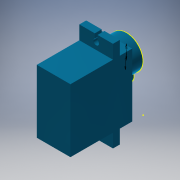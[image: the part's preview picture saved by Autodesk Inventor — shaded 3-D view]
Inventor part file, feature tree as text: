
AUTODESK INVENTOR PART (.ipt)
format: ipt  version: 2016 SP2 (Build 200236200, 236)  size: 158,208 bytes
history: native  units: mm
features: sketch x5, projected_geometry x5, extrude x4, plane x1, mirror x1
ambient origin geometry x8: Origin, YZ Plane, XZ Plane, XY Plane, X Axis, Y Axis, Z Axis, Center Point
bodies: Solid1 (feature_tree)
feature tree (16):
  extrude  "Extrusion1"  Depth=23.0mm
  extrude  "Extrusion2"  Depth=4.5mm
  extrude  "Extrusion3"  Depth=5.0mm TaperAngle=0.0deg
  plane  "Work Plane1"
  mirror  "Mirror1"
  extrude  "Extrusion4"  Depth=2.0mm
  sketch  "Sketch5"  dims[d10=0.5mm d11=3.5mm d12=6.75mm d13=0.0mm d14=6.0mm d15=6.5mm d16=5.5mm d17=4.0mm d18=0.0mm d19=6.0mm d20=5.0mm]
  sketch  "Sketch1"  dims[d0=12.25mm d1=23.0mm]
  sketch  "Sketch2"  dims[d2=22.5mm d3=0.0mm d4=4.5mm]
  projected_geometry  "Projected Loop1"
  sketch  "Sketch3"  dims[d5=2.5mm d6=5.0mm d7=0.0mm]
  projected_geometry  "Projected Loop2"
  sketch  "Sketch4"  dims[d8=0.5mm d9=2.0mm]
  projected_geometry  "Projected Loop3"
  projected_geometry  "Projected Loop4"
  projected_geometry  "Project Cut Edges1"
